# Revit family: Coupling-Expansion_Joint-Champion_Couplings-R1900-NH_Series
name_source: partatom
category: Pipe Fittings
revit_build: Autodesk Revit 2014 (Build: 20130308_1515(x64)
units: mm (PartAtom-declared; Revit-internal decimal feet)

## types (5) — shared parameters
Assembly Code = D2090800
CW Connection = Yes
Description = MIFAB® Series of R1900-NH neoprene expansion joints are manufactured with Type 300 stainless steel clamps
operated by Type 300 5/16” screws.
HW Connection = No
Manufacturer = Champion Couplings
Material = Synthetic Rubber-Champion Couplings-Neoprene
Model = R1900-NH
Price = Prices may vary. Please consult Manufacturer Representative for most up-to-date price list.
Product Documentation Link = http://www.mifab.com
Product Page URL = http://www.mifab.com
Standard Listings & Approval = CSA Approved, U.P.C. Approved
URL = http://www.mifab.com
Vent Connection = No
Warranty Information = 1 Year Warranty
Waste Connection = No

## per-type parameters (varying)
| type | Height | List Price (Each Piece) | Pipe Connection Diameter | Pipe Size Description | Tick Size | Width A | Width B |
| R1902-NH | 7.125" | $16.75 | 2.000" | 2" x 2" | 0.880" | 2.200" | 2.200" |
| R1903-NH | 8.125" | $18.00 | 3.000" | 3" x 3" | 1.320" | 3.300" | 3.300" |
| R1904-NH | 8.625" | $22.75 | 4.000" | 4" x 4" | 1.760" | 4.400" | 4.400" |
| R1906-NH | 8.625" | $30.00 | 6.000" | 6" x 6" | 2.640" | 6.600" | 6.600" |
| R1908-NH | 11.000" | $50.00 | 8.000" | 8" x 8" | 3.520" | 8.800" | 8.800" |

## geometry (parser evidence)
native form markers: Sweep x3
no freeform markers — native parametric forms only
